FCSTD DOCUMENT  (FreeCAD 0.21R33771 (Git))
Label: Makita LXT  - 18V - Bottom
License: Creative Commons Attribution 4.0
LicenseURL: https://creativecommons.org/licenses/by/4.0/
objects: Mesh::Feature×3, Sketcher::SketchObject×1, PartDesign::Body×1
note: 2 computed .brp shape members not serialized (recipe doc carries the construction recipe); baked Part::Feature solids carry a one-line shape summary decoded from their .brp

FEATURE [Mesh::Feature] XT60_top
  Placement = pos=(-27.47,40,-11) rot=(0,0,1;0rad)
FEATURE [Mesh::Feature] XT60_top001
  Placement = pos=(-27.47,-40,2) rot=(0,0,1;0rad)
FEATURE [Sketcher::SketchObject] Sketch
  FullyConstrained = true
  MapMode = 5
  Support = -> [XY_Plane]
  sketch-geometry (16):
    g0: ArcOfCircle CenterX=259.65 CenterY=40 CenterZ=0 NormalX=0 NormalY=0 NormalZ=1 AngleXU=0 Radius=259.65 StartAngle=3.05831 EndAngle=3.14159
    g1: ArcOfCircle CenterX=15.6319 CenterY=60.3702 CenterZ=0 NormalX=0 NormalY=0 NormalZ=1 AngleXU=0 Radius=14.7831 StartAngle=1.7292 EndAngle=3.05831
    g2: LineSegment StartX=20 StartY=75.5 StartZ=0 EndX=64.2 EndY=75.5 EndZ=0
    g3: ArcOfCircle CenterX=64.2 CenterY=48.7705 CenterZ=0 NormalX=0 NormalY=0 NormalZ=1 AngleXU=0 Radius=26.7295 StartAngle=0.24292 EndAngle=1.5708
    g4: ArcOfCircle CenterX=28.8084 CenterY=40 CenterZ=0 NormalX=0 NormalY=0 NormalZ=1 AngleXU=0 Radius=63.1916 StartAngle=0 EndAngle=0.24292
    g5: ArcOfCircle CenterX=20 CenterY=33.0247 CenterZ=0 NormalX=0 NormalY=0 NormalZ=1 AngleXU=0 Radius=42.4753 StartAngle=1.5708 EndAngle=1.7292
    g6: LineSegment StartX=0 StartY=40 StartZ=0 EndX=0 EndY=0 EndZ=0
    g7: LineSegment StartX=92 StartY=40 StartZ=0 EndX=92 EndY=0 EndZ=0
    g8: ArcOfCircle CenterX=259.65 CenterY=-40 CenterZ=0 NormalX=0 NormalY=0 NormalZ=1 AngleXU=0 Radius=259.65 StartAngle=3.14159 EndAngle=3.22488
    g9: ArcOfCircle CenterX=15.6319 CenterY=-60.3702 CenterZ=0 NormalX=0 NormalY=0 NormalZ=1 AngleXU=0 Radius=14.7831 StartAngle=3.22488 EndAngle=4.55399
    g10: LineSegment StartX=20 StartY=-75.5 StartZ=0 EndX=64.2 EndY=-75.5 EndZ=0
    g11: ArcOfCircle CenterX=64.2 CenterY=-48.7705 CenterZ=0 NormalX=0 NormalY=0 NormalZ=1 AngleXU=0 Radius=26.7295 StartAngle=4.71239 EndAngle=6.04026
    g12: ArcOfCircle CenterX=28.8084 CenterY=-40 CenterZ=0 NormalX=0 NormalY=0 NormalZ=1 AngleXU=0 Radius=63.1916 StartAngle=6.04026 EndAngle=6.28319
    g13: ArcOfCircle CenterX=20 CenterY=-33.0247 CenterZ=0 NormalX=0 NormalY=0 NormalZ=1 AngleXU=0 Radius=42.4753 StartAngle=4.55399 EndAngle=4.71239
    g14: LineSegment StartX=0 StartY=-40 StartZ=0 EndX=0 EndY=0 EndZ=0
    g15: LineSegment StartX=92 StartY=-40 StartZ=0 EndX=92 EndY=0 EndZ=0
  constraints (46):
    c: Horizontal(g2)
    c: DistanceX(g2) = 20
    c: DistanceX(g2,g2) = 44.2
    c: Tangent(g4,g3) = -1.5708
    c: Tangent(g3,g2) = 1.5708
    c: Tangent(g1,g0) = -1.5708
    c: Tangent(g5,g2) = 1.5708
    c: Tangent(g5,g1) = -1.5708
    c: DistanceX(g0) = 0.9
    c: DistanceX(g1) = 13.3
    c: Coincident(g6,g-1)
    c: Vertical(g6)
    c: PointOnObject(g7,g-1)
    c: Vertical(g7)
    c: Equal(g7,g6)
    c: DistanceY(g0) = 40
    c: DistanceX(g4) = 92
    c: Tangent(g7,g4) = 1.5708
    c: Tangent(g6,g0) = -1.5708
    c: Horizontal(g10)
    c: Tangent(g12,g11) = -1.5708
    c: Tangent(g11,g10) = -1.5708
    c: Tangent(g9,g8) = -1.5708
    c: Tangent(g13,g10) = -1.5708
    c: Tangent(g13,g9) = -1.5708
    c: Vertical(g14)
    c: Vertical(g15)
    c: Equal(g15,g14)
    c: Tangent(g15,g12) = -1.5708
    c: Tangent(g14,g8) = 1.5708
    c: Radius(g8) = 259.65  'Radius1'
    c: Radius(g9) = 14.7831  'Radius2'
    c: Radius(g13) = 42.4753  'Radius3'
    c: Radius(g11) = 26.7295  'Radius4'
    c: Radius(g12) = 63.1916  'Radius5'
    c: Coincident(g14,g6)
    c: Coincident(g15,g7)
    c: Equal(g12,g4)
    c: Equal(g11,g3)
    c: Equal(g5,g13)
    c: Equal(g9,g1)
    c: Symmetric(g8,g0,g-1)
    c: Symmetric(g1,g9,g-1)
    c: DistanceY(g0,g0) = 21.6
    c: DistanceY(g0,g2) = 35.5
    c: DistanceY(g4,g3) = 15.2
FEATURE [PartDesign::Body] Body  label="Makita 18B x 2 base"
  Group = -> [Sketch]
  Origin = -> Origin
FEATURE [Mesh::Feature] makita_t_mount_M3
  Placement = pos=(-27.47,-40,0) rot=(0,0,1;0rad)
